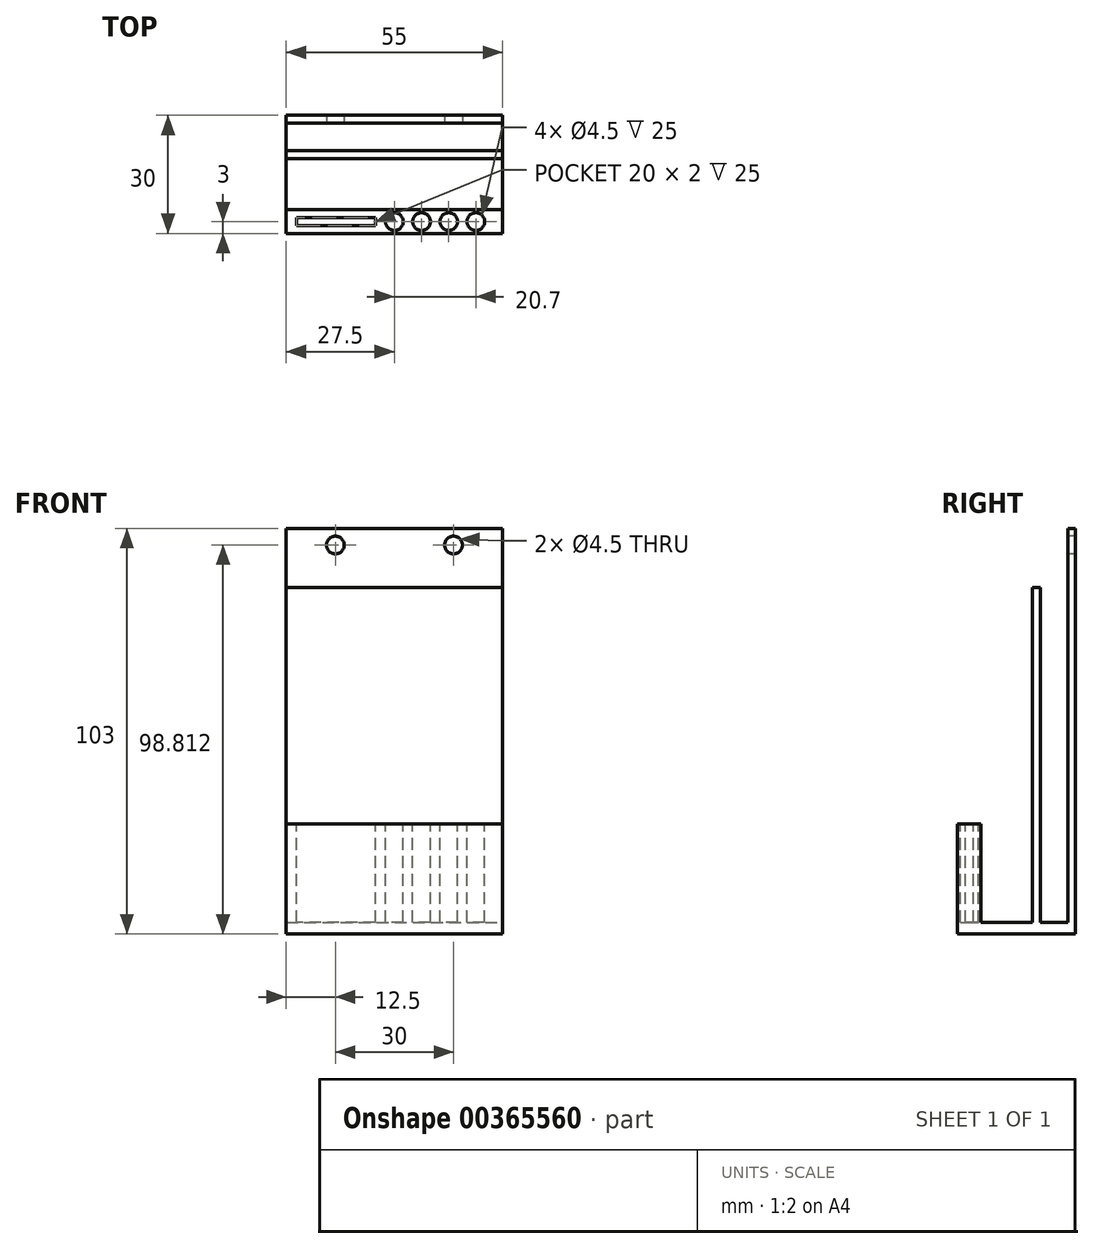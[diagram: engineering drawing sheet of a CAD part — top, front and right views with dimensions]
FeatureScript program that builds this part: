
annotation { "Feature Type Name" : "Feature", "Feature Type Description" : "" }
export const myFeature = defineFeature(function(context is Context, id is Id, definition is map)
    precondition{}
    {
        {
            var Q0;
            Q0=qCreatedBy(makeId("Top.planeOp"),FACE);
            var sketch = newSketch(context, id + "F0", { "sketchPlane" : qUnion([Q0])});
            skLineSegment(sketch, "E0.bottom", {"start": v(27.5, -15) * mm, "end": v(-27.5, -15) * mm});
            skLineSegment(sketch, "E0.top", {"start": v(27.5, 15) * mm, "end": v(-27.5, 15) * mm});
            skLineSegment(sketch, "E0.left", {"start": v(27.5, -15) * mm, "end": v(27.5, 15) * mm});
            skLineSegment(sketch, "E0.right", {"start": v(-27.5, -15) * mm, "end": v(-27.5, 15) * mm});
            skPoint(sketch, "E0.middle", {"position": v(0, 0) * mm});
            skSolve(sketch);
        }
        {
            var Q0;
            Q0=makeQuery(id+"F0.imprint","IMPRINT",FACE,{"disambiguationData":[TD([[makeQuery(id+"F0.imprint","IMPRINT",EDGE,{"derivedFrom":sQuery(id+"F0.wireOp",EDGE,"E0.bottom")}),-1.0]])]});
            extrude(context, id + "F1", {"entities" : qUnion([Q0]), "depth" : 3 * mm});
        }
        {
            var Q0;
            Q0=makeQuery(id+"F1.opExtrude","CAP_FACE",FACE,{"disambiguationData":[OSD([sQuery(id+"F0.wireOp",EDGE,"E0.bottom"),sQuery(id+"F0.wireOp",EDGE,"E0.top"),sQuery(id+"F0.wireOp",EDGE,"E0.left"),sQuery(id+"F0.wireOp",EDGE,"E0.right")])],"isStart":false});
            var sketch = newSketch(context, id + "F2", { "sketchPlane" : qUnion([Q0])});
            skLineSegment(sketch, "E1.bottom", {"start": v(-27.5, 15) * mm, "end": v(27.5, 15) * mm});
            skLineSegment(sketch, "E1.top", {"start": v(-27.5, 13) * mm, "end": v(27.5, 13) * mm});
            skLineSegment(sketch, "E1.left", {"start": v(-27.5, 15) * mm, "end": v(-27.5, 13) * mm});
            skLineSegment(sketch, "E1.right", {"start": v(27.5, 15) * mm, "end": v(27.5, 13) * mm});
            skLineSegment(sketch, "E2.bottom", {"start": v(-27.5, 13) * mm, "end": v(-25.5, 13) * mm});
            skLineSegment(sketch, "E2.top", {"start": v(-27.5, 6) * mm, "end": v(-25.5, 6) * mm});
            skLineSegment(sketch, "E2.left", {"start": v(-27.5, 13) * mm, "end": v(-27.5, 6) * mm});
            skLineSegment(sketch, "E2.right", {"start": v(-25.5, 13) * mm, "end": v(-25.5, 6) * mm});
            skLineSegment(sketch, "E3.bottom", {"start": v(27.5, 13) * mm, "end": v(25.5, 13) * mm});
            skLineSegment(sketch, "E3.top", {"start": v(27.5, 6) * mm, "end": v(25.5, 6) * mm});
            skLineSegment(sketch, "E3.left", {"start": v(27.5, 13) * mm, "end": v(27.5, 6) * mm});
            skLineSegment(sketch, "E3.right", {"start": v(25.5, 13) * mm, "end": v(25.5, 6) * mm});
            skLineSegment(sketch, "E4.bottom", {"start": v(-27.5, 6) * mm, "end": v(27.5, 6) * mm});
            skLineSegment(sketch, "E4.top", {"start": v(-27.5, 4) * mm, "end": v(27.5, 4) * mm});
            skLineSegment(sketch, "E4.left", {"start": v(-27.5, 6) * mm, "end": v(-27.5, 4) * mm});
            skLineSegment(sketch, "E4.right", {"start": v(27.5, 6) * mm, "end": v(27.5, 4) * mm});
            skLineSegment(sketch, "E5.bottom", {"start": v(-27.5, -15) * mm, "end": v(27.5, -15) * mm});
            skLineSegment(sketch, "E5.top", {"start": v(-27.5, -9) * mm, "end": v(27.5, -9) * mm});
            skLineSegment(sketch, "E5.left", {"start": v(-27.5, -15) * mm, "end": v(-27.5, -9) * mm});
            skLineSegment(sketch, "E5.right", {"start": v(27.5, -15) * mm, "end": v(27.5, -9) * mm});
            skLineSegment(sketch, "E6.bottom", {"start": v(-27.5, 4) * mm, "end": v(-25.5, 4) * mm});
            skLineSegment(sketch, "E6.top", {"start": v(-27.5, -9) * mm, "end": v(-25.5, -9) * mm});
            skLineSegment(sketch, "E6.left", {"start": v(-27.5, 4) * mm, "end": v(-27.5, -9) * mm});
            skLineSegment(sketch, "E6.right", {"start": v(-25.5, 4) * mm, "end": v(-25.5, -9) * mm});
            skLineSegment(sketch, "E7.bottom", {"start": v(27.5, 4) * mm, "end": v(25.5, 4) * mm});
            skLineSegment(sketch, "E7.top", {"start": v(27.5, -9) * mm, "end": v(25.5, -9) * mm});
            skLineSegment(sketch, "E7.left", {"start": v(27.5, 4) * mm, "end": v(27.5, -9) * mm});
            skLineSegment(sketch, "E7.right", {"start": v(25.5, 4) * mm, "end": v(25.5, -9) * mm});
            skSolve(sketch);
        }
        {
            var Q0;
            Q0=makeQuery(id+"F2.imprint","IMPRINT",FACE,{"disambiguationData":[TD([[makeQuery(id+"F2.imprint","IMPRINT",EDGE,{"derivedFrom":sQuery(id+"F2.wireOp",EDGE,"E1.bottom")}),1.0]])]});
            extrude(context, id + "F3", {"entities" : qUnion([Q0]), "operationType" : NewBodyOperationType.ADD, "depth" : 100 * mm});
        }
        {
            var Q0;
            Q0=makeQuery(id+"F2.imprint","IMPRINT",FACE,{"disambiguationData":[TD([[makeQuery(id+"F2.imprint","IMPRINT",EDGE,{"derivedFrom":sQuery(id+"F2.wireOp",EDGE,"E2.bottom")}),-1.0]])]});
            var Q1;
            Q1=makeQuery(id+"F2.imprint","IMPRINT",FACE,{"disambiguationData":[TD([[makeQuery(id+"F2.imprint","IMPRINT",EDGE,{"derivedFrom":sQuery(id+"F2.wireOp",EDGE,"E4.top")}),1.0]])]});
            var Q2;
            Q2=makeQuery(id+"F2.imprint","IMPRINT",FACE,{"disambiguationData":[TD([[makeQuery(id+"F2.imprint","IMPRINT",EDGE,{"derivedFrom":sQuery(id+"F2.wireOp",EDGE,"E3.bottom")}),1.0]])]});
            extrude(context, id + "F4", {"entities" : qUnion([Q0, Q1, Q2]), "operationType" : NewBodyOperationType.ADD, "depth" : 85 * mm});
        }
        {
            var Q0;
            Q0=makeQuery(id+"F2.imprint","IMPRINT",FACE,{"disambiguationData":[TD([[makeQuery(id+"F2.imprint","IMPRINT",EDGE,{"derivedFrom":sQuery(id+"F2.wireOp",EDGE,"E7.bottom")}),1.0]])]});
            var Q1;
            Q1=makeQuery(id+"F2.imprint","IMPRINT",FACE,{"disambiguationData":[TD([[makeQuery(id+"F2.imprint","IMPRINT",EDGE,{"derivedFrom":sQuery(id+"F2.wireOp",EDGE,"E5.bottom")}),-1.0]])]});
            var Q2;
            Q2=makeQuery(id+"F2.imprint","IMPRINT",FACE,{"disambiguationData":[TD([[makeQuery(id+"F2.imprint","IMPRINT",EDGE,{"derivedFrom":sQuery(id+"F2.wireOp",EDGE,"E6.bottom")}),-1.0]])]});
            extrude(context, id + "F5", {"entities" : qUnion([Q0, Q1, Q2]), "operationType" : NewBodyOperationType.ADD, "depth" : 25 * mm});
        }
        {
            var Q0;
            Q0=makeQuery(id+"F5.opExtrude","CAP_FACE",FACE,{"disambiguationData":[OSD([sQuery(id+"F2.wireOp",EDGE,"E5.bottom"),sQuery(id+"F2.wireOp",EDGE,"E5.top"),sQuery(id+"F2.wireOp",EDGE,"E5.left"),sQuery(id+"F2.wireOp",EDGE,"E5.right"),sQuery(id+"F2.wireOp",EDGE,"E6.bottom"),sQuery(id+"F2.wireOp",EDGE,"E6.left"),sQuery(id+"F2.wireOp",EDGE,"E6.right"),sQuery(id+"F2.wireOp",EDGE,"E7.bottom"),sQuery(id+"F2.wireOp",EDGE,"E7.left"),sQuery(id+"F2.wireOp",EDGE,"E7.right")])],"isStart":false});
            var sketch = newSketch(context, id + "F6", { "sketchPlane" : qUnion([Q0])});
            skLineSegment(sketch, "E8", {"start": v(0, -15) * mm, "end": v(0, -9) * mm, "construction": true});
            skLineSegment(sketch, "E9", {"start": v(-27.5, -12) * mm, "end": v(27.5, -12) * mm, "construction": true});
            skPoint(sketch, "E9.startSnap0", {"position": v(0, -12) * mm});
            skCircle(sketch, "E10", {"center": v(0, -12) * mm, "radius": 2.25 * mm});
            skCircle(sketch, "E11", {"center": v(6.9, -12) * mm, "radius": 2.25 * mm});
            skCircle(sketch, "E12", {"center": v(13.8, -12) * mm, "radius": 2.25 * mm});
            skCircle(sketch, "E13", {"center": v(20.7, -12) * mm, "radius": 2.25 * mm});
            skLineSegment(sketch, "E14.bottom", {"start": v(-4.83, -13) * mm, "end": v(-24.83, -13) * mm});
            skLineSegment(sketch, "E14.top", {"start": v(-4.83, -11) * mm, "end": v(-24.83, -11) * mm});
            skLineSegment(sketch, "E14.left", {"start": v(-4.83, -13) * mm, "end": v(-4.83, -11) * mm});
            skLineSegment(sketch, "E14.right", {"start": v(-24.83, -13) * mm, "end": v(-24.83, -11) * mm});
            skPoint(sketch, "E14.middle", {"position": v(-14.83, -12) * mm});
            skSolve(sketch);
        }
        {
            var Q0;
            Q0=makeQuery(id+"F6.imprint","IMPRINT",FACE,{"disambiguationData":[TD([[makeQuery(id+"F6.imprint","IMPRINT",EDGE,{"derivedFrom":sQuery(id+"F6.wireOp",EDGE,"E10")}),1.0]])]});
            var Q1;
            Q1=makeQuery(id+"F6.imprint","IMPRINT",FACE,{"disambiguationData":[TD([[makeQuery(id+"F6.imprint","IMPRINT",EDGE,{"derivedFrom":sQuery(id+"F6.wireOp",EDGE,"E11")}),1.0]])]});
            var Q2;
            Q2=makeQuery(id+"F6.imprint","IMPRINT",FACE,{"disambiguationData":[TD([[makeQuery(id+"F6.imprint","IMPRINT",EDGE,{"derivedFrom":sQuery(id+"F6.wireOp",EDGE,"E12")}),1.0]])]});
            var Q3;
            Q3=makeQuery(id+"F6.imprint","IMPRINT",FACE,{"disambiguationData":[TD([[makeQuery(id+"F6.imprint","IMPRINT",EDGE,{"derivedFrom":sQuery(id+"F6.wireOp",EDGE,"E13")}),1.0]])]});
            var Q4;
            Q4=makeQuery(id+"F6.imprint","IMPRINT",FACE,{"disambiguationData":[TD([[makeQuery(id+"F6.imprint","IMPRINT",EDGE,{"derivedFrom":sQuery(id+"F6.wireOp",EDGE,"E14.bottom")}),-1.0]])]});
            extrude(context, id + "F7", {"entities" : qUnion([Q0, Q1, Q2, Q3, Q4]), "operationType" : NewBodyOperationType.REMOVE, "oppositeDirection" : true, "depth" : 25 * mm});
        }
        {
            var Q0;
            Q0=makeQuery(id+"F3.opExtrude","SWEPT_FACE",FACE,{"disambiguationData":[OSD([sQuery(id+"F2.wireOp",EDGE,"E1.top"),sQuery(id+"F2.wireOp",EDGE,"E2.bottom"),sQuery(id+"F2.wireOp",EDGE,"E3.bottom")])]});
            var sketch = newSketch(context, id + "F8", { "sketchPlane" : qUnion([Q0])});
            skCircle(sketch, "E15", {"center": v(-15, 98.81) * mm, "radius": 2.25 * mm});
            skCircle(sketch, "E16", {"center": v(15, 98.81) * mm, "radius": 2.25 * mm});
            skSolve(sketch);
        }
        {
            var Q0;
            Q0=makeQuery(id+"F8.imprint","IMPRINT",FACE,{"disambiguationData":[TD([[makeQuery(id+"F8.imprint","IMPRINT",EDGE,{"derivedFrom":sQuery(id+"F8.wireOp",EDGE,"E15")}),1.0]])]});
            var Q1;
            Q1=makeQuery(id+"F8.imprint","IMPRINT",FACE,{"disambiguationData":[TD([[makeQuery(id+"F8.imprint","IMPRINT",EDGE,{"derivedFrom":sQuery(id+"F8.wireOp",EDGE,"E16")}),1.0]])]});
            extrude(context, id + "F9", {"entities" : qUnion([Q0, Q1]), "operationType" : NewBodyOperationType.REMOVE, "endBound" : BoundingType.THROUGH_ALL, "oppositeDirection" : true, "depth" : 25 * mm});
        }
    });
